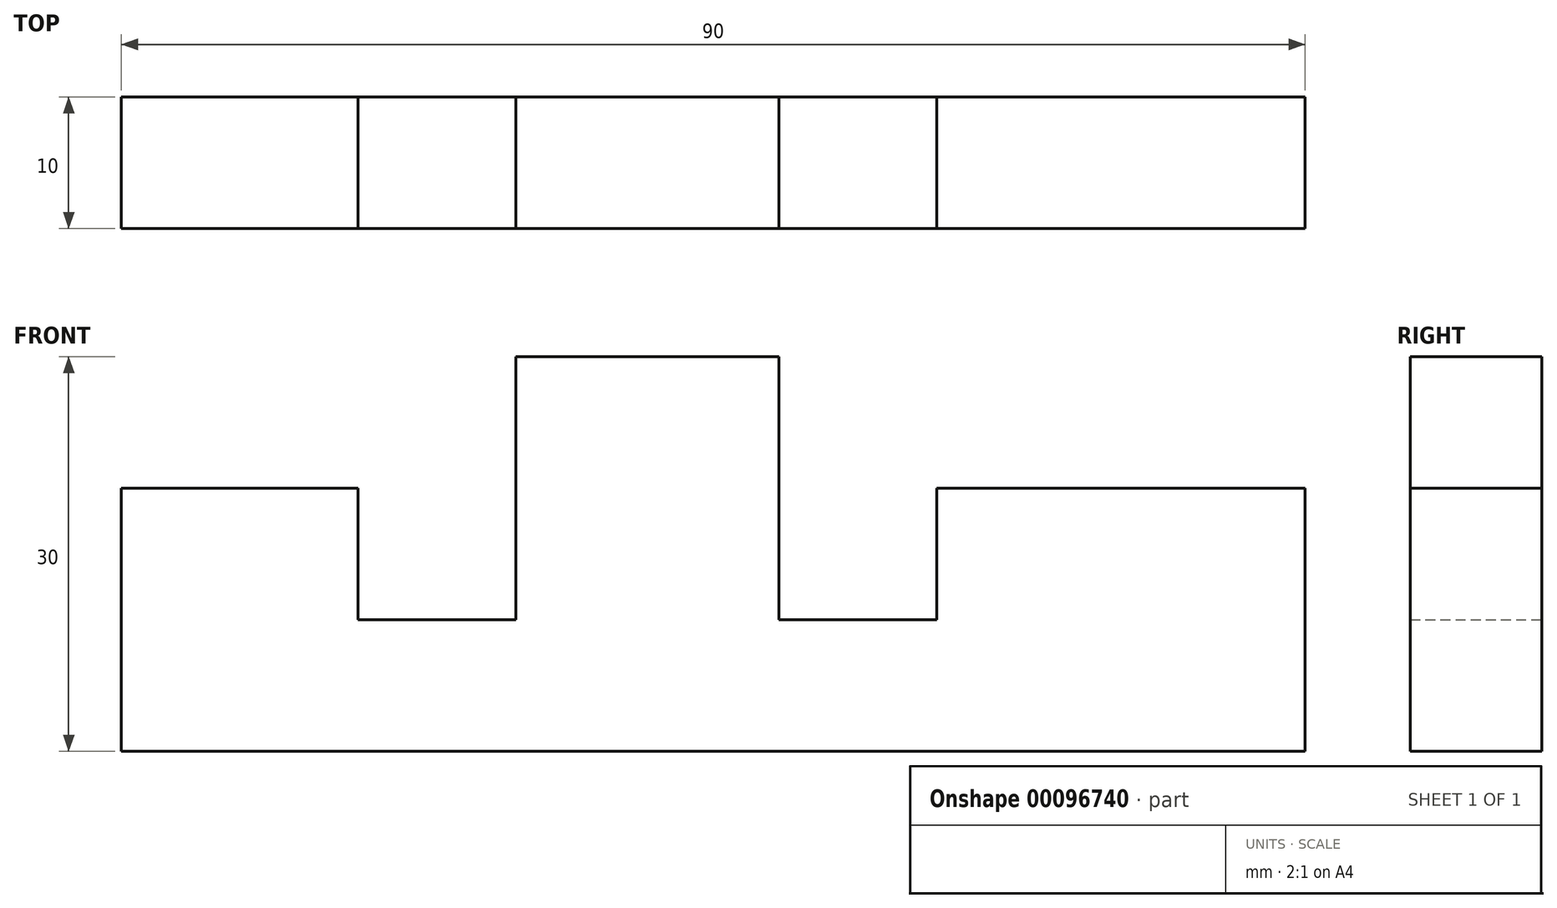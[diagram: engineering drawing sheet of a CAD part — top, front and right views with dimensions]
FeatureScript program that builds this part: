
annotation { "Feature Type Name" : "Feature", "Feature Type Description" : "" }
export const myFeature = defineFeature(function(context is Context, id is Id, definition is map)
    precondition{}
    {
        {
            var Q0;
            Q0=qCreatedBy(makeId("Front.planeOp"),FACE);
            var sketch = newSketch(context, id + "F0", { "sketchPlane" : qUnion([Q0])});
            skLineSegment(sketch, "E0", {"start": v(0, 0) * mm, "end": v(90, 0) * mm});
            skLineSegment(sketch, "E1", {"start": v(0, 0) * mm, "end": v(0, 20) * mm});
            skLineSegment(sketch, "E2", {"start": v(0, 20) * mm, "end": v(18, 20) * mm});
            skLineSegment(sketch, "E3", {"start": v(18, 20) * mm, "end": v(18, 10) * mm});
            skLineSegment(sketch, "E4", {"start": v(18, 10) * mm, "end": v(30, 10) * mm});
            skLineSegment(sketch, "E5", {"start": v(30, 10) * mm, "end": v(30, 30) * mm});
            skLineSegment(sketch, "E6", {"start": v(30, 30) * mm, "end": v(50, 30) * mm});
            skLineSegment(sketch, "E7", {"start": v(50, 30) * mm, "end": v(50, 10) * mm});
            skLineSegment(sketch, "E8", {"start": v(50, 10) * mm, "end": v(62, 10) * mm});
            skLineSegment(sketch, "E9", {"start": v(62, 10) * mm, "end": v(62, 20) * mm});
            skLineSegment(sketch, "E10", {"start": v(62, 20) * mm, "end": v(90, 20) * mm});
            skLineSegment(sketch, "E11", {"start": v(90, 20) * mm, "end": v(90, 0) * mm});
            skSolve(sketch);
        }
        {
            var Q0;
            Q0 = qSketchRegion(id + "F0", true);
            extrude(context, id + "F1", {"entities" : qUnion([Q0]), "depth" : 10 * mm});
        }
    });
